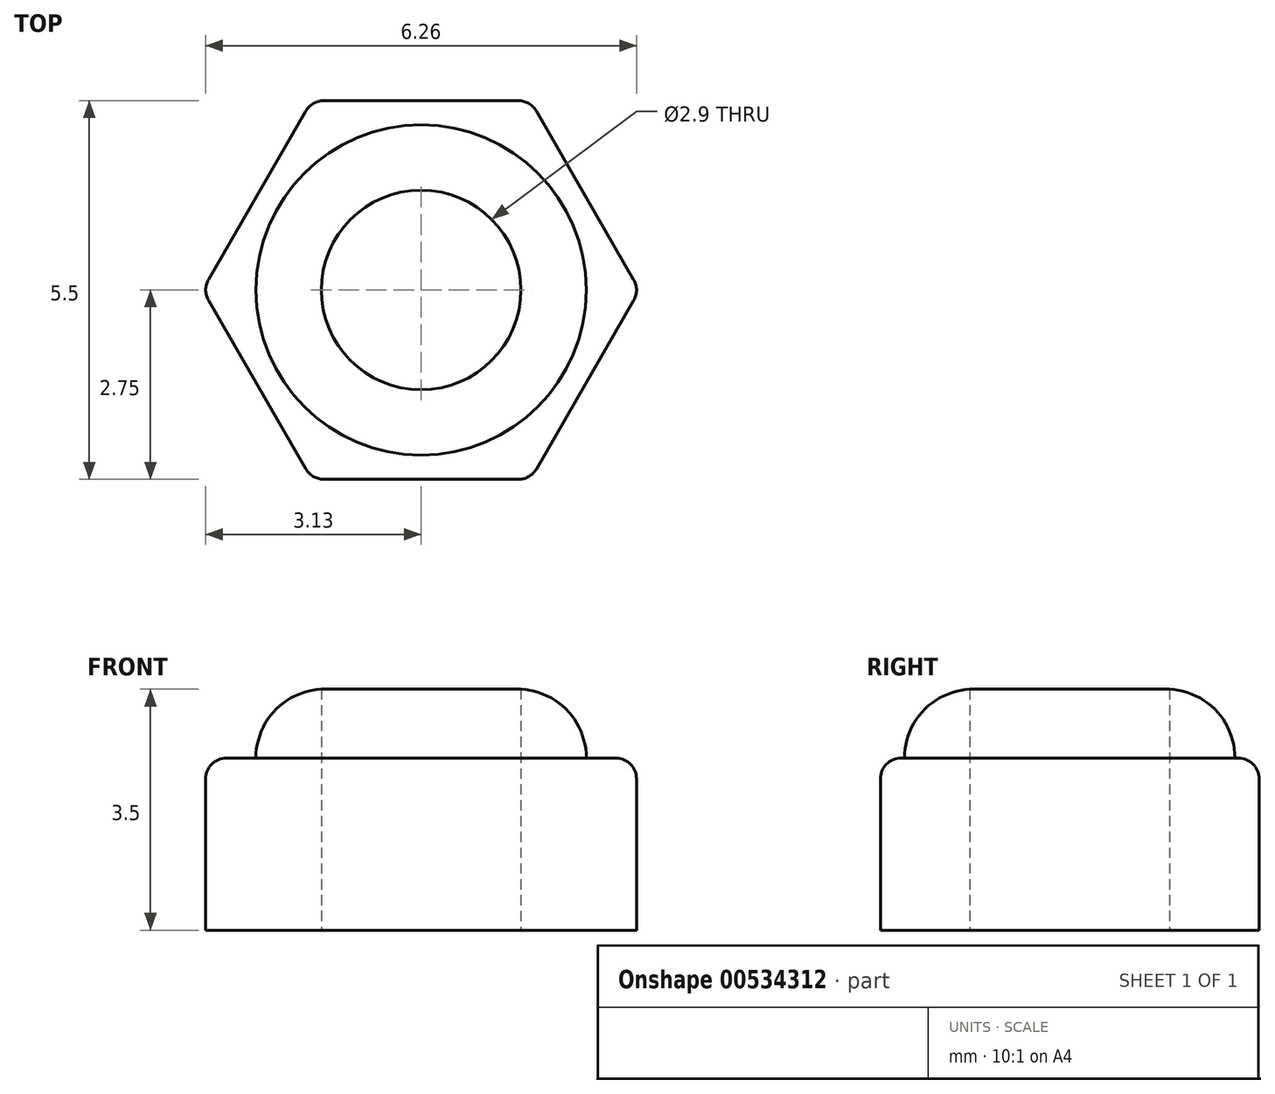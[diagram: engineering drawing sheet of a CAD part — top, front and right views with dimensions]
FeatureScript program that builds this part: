
annotation { "Feature Type Name" : "Feature", "Feature Type Description" : "" }
export const myFeature = defineFeature(function(context is Context, id is Id, definition is map)
    precondition{}
    {
        {
            var Q0;
            Q0=qCreatedBy(makeId("Top.planeOp"),FACE);
            var sketch = newSketch(context, id + "F0", { "sketchPlane" : qUnion([Q0])});
            skCircle(sketch, "E0", {"center": v(0, 0) * mm, "radius": 1.45 * mm});
            skCircle(sketch, "E1.cCircle", {"center": v(0, 0) * mm, "radius": 3.18 * mm, "construction": true});
            skLineSegment(sketch, "E1.0", {"start": v(1.59, -2.75) * mm, "end": v(-1.59, -2.75) * mm});
            skLineSegment(sketch, "E1.1", {"start": v(-1.59, -2.75) * mm, "end": v(-3.18, 0) * mm});
            skLineSegment(sketch, "E1.2", {"start": v(-3.18, 0) * mm, "end": v(-1.59, 2.75) * mm});
            skLineSegment(sketch, "E1.3", {"start": v(-1.59, 2.75) * mm, "end": v(1.59, 2.75) * mm});
            skLineSegment(sketch, "E1.4", {"start": v(1.59, 2.75) * mm, "end": v(3.18, 0) * mm});
            skLineSegment(sketch, "E1.5", {"start": v(3.18, 0) * mm, "end": v(1.59, -2.75) * mm});
            skSolve(sketch);
        }
        {
            var Q0;
            Q0=qSketchRegion(id+"F0",true);
            extrude(context, id + "F1", {"entities" : qUnion([Q0]), "depth" : 2.5 * mm});
        }
        {
            var Q0;
            Q0=qCreatedBy(makeId("Top.planeOp"),FACE);
            cPlane(context, id + "F2", {"entities" : qUnion([Q0]), "cplaneType" : CPlaneType.OFFSET, "offset" : 2.5 * mm, "width" : 150 * mm, "height" : 150 * mm});
        }
        {
            var Q0;
            Q0=qCreatedBy(id+"F2.planeOp",FACE);
            var sketch = newSketch(context, id + "F3", { "sketchPlane" : qUnion([Q0])});
            skCircle(sketch, "E2", {"center": v(0, 0) * mm, "radius": 1.45 * mm});
            skCircle(sketch, "E3", {"center": v(0, 0) * mm, "radius": 2.4 * mm});
            skSolve(sketch);
        }
        {
            var Q0;
            Q0=qSketchRegion(id+"F3",true);
            extrude(context, id + "F4", {"entities" : qUnion([Q0]), "operationType" : NewBodyOperationType.ADD, "depth" : 1 * mm});
        }
        {
            var Q0;
            Q0=makeQuery(id+"F1.opExtrude","CAP_EDGE",EDGE,{"disambiguationData":[OSD([sQuery(id+"F0.wireOp",EDGE,"E1.1")])],"isStart":false});
            var Q1;
            Q1=makeQuery(id+"F1.opExtrude","CAP_EDGE",EDGE,{"disambiguationData":[OSD([sQuery(id+"F0.wireOp",EDGE,"E1.2")])],"isStart":false});
            var Q2;
            Q2=makeQuery(id+"F1.opExtrude","CAP_EDGE",EDGE,{"disambiguationData":[OSD([sQuery(id+"F0.wireOp",EDGE,"E1.3")])],"isStart":false});
            var Q3;
            Q3=makeQuery(id+"F1.opExtrude","CAP_EDGE",EDGE,{"disambiguationData":[OSD([sQuery(id+"F0.wireOp",EDGE,"E1.4")])],"isStart":false});
            var Q4;
            Q4=makeQuery(id+"F1.opExtrude","CAP_EDGE",EDGE,{"disambiguationData":[OSD([sQuery(id+"F0.wireOp",EDGE,"E1.5")])],"isStart":false});
            var Q5;
            Q5=makeQuery(id+"F1.opExtrude","CAP_EDGE",EDGE,{"disambiguationData":[OSD([sQuery(id+"F0.wireOp",EDGE,"E1.0")])],"isStart":false});
            var Q6;
            Q6=makeQuery(id+"F1.opExtrude","SWEPT_EDGE",EDGE,{"disambiguationData":[OSD([sQuery(id+"F0.wireOp",EDGE,"E1.4"),sQuery(id+"F0.wireOp",EDGE,"E1.5")])]});
            var Q7;
            Q7=makeQuery(id+"F1.opExtrude","SWEPT_EDGE",EDGE,{"disambiguationData":[OSD([sQuery(id+"F0.wireOp",EDGE,"E1.3"),sQuery(id+"F0.wireOp",EDGE,"E1.4")])]});
            var Q8;
            Q8=makeQuery(id+"F1.opExtrude","SWEPT_EDGE",EDGE,{"disambiguationData":[OSD([sQuery(id+"F0.wireOp",EDGE,"E1.2"),sQuery(id+"F0.wireOp",EDGE,"E1.3")])]});
            var Q9;
            Q9=makeQuery(id+"F1.opExtrude","SWEPT_EDGE",EDGE,{"disambiguationData":[OSD([sQuery(id+"F0.wireOp",EDGE,"E1.1"),sQuery(id+"F0.wireOp",EDGE,"E1.2")])]});
            var Q10;
            Q10=makeQuery(id+"F1.opExtrude","SWEPT_EDGE",EDGE,{"disambiguationData":[OSD([sQuery(id+"F0.wireOp",EDGE,"E1.0"),sQuery(id+"F0.wireOp",EDGE,"E1.1")])]});
            var Q11;
            Q11=makeQuery(id+"F1.opExtrude","SWEPT_EDGE",EDGE,{"disambiguationData":[OSD([sQuery(id+"F0.wireOp",EDGE,"E1.0"),sQuery(id+"F0.wireOp",EDGE,"E1.5")])]});
            fillet(context, id + "F5", {"entities" : qUnion([Q0, Q1, Q2, Q3, Q4, Q5, Q6, Q7, Q8, Q9, Q10, Q11]), "radius" : .3 * mm, "tangentPropagation" : true, "allowEdgeOverflow" : false});
        }
        {
            var Q0;
            Q0=makeQuery(id+"F4.opExtrude","CAP_EDGE",EDGE,{"disambiguationData":[OSD([sQuery(id+"F3.wireOp",EDGE,"E3")])],"isStart":false});
            fillet(context, id + "F6", {"entities" : qUnion([Q0]), "radius" : 1 * mm, "tangentPropagation" : true, "allowEdgeOverflow" : false});
        }
    });
